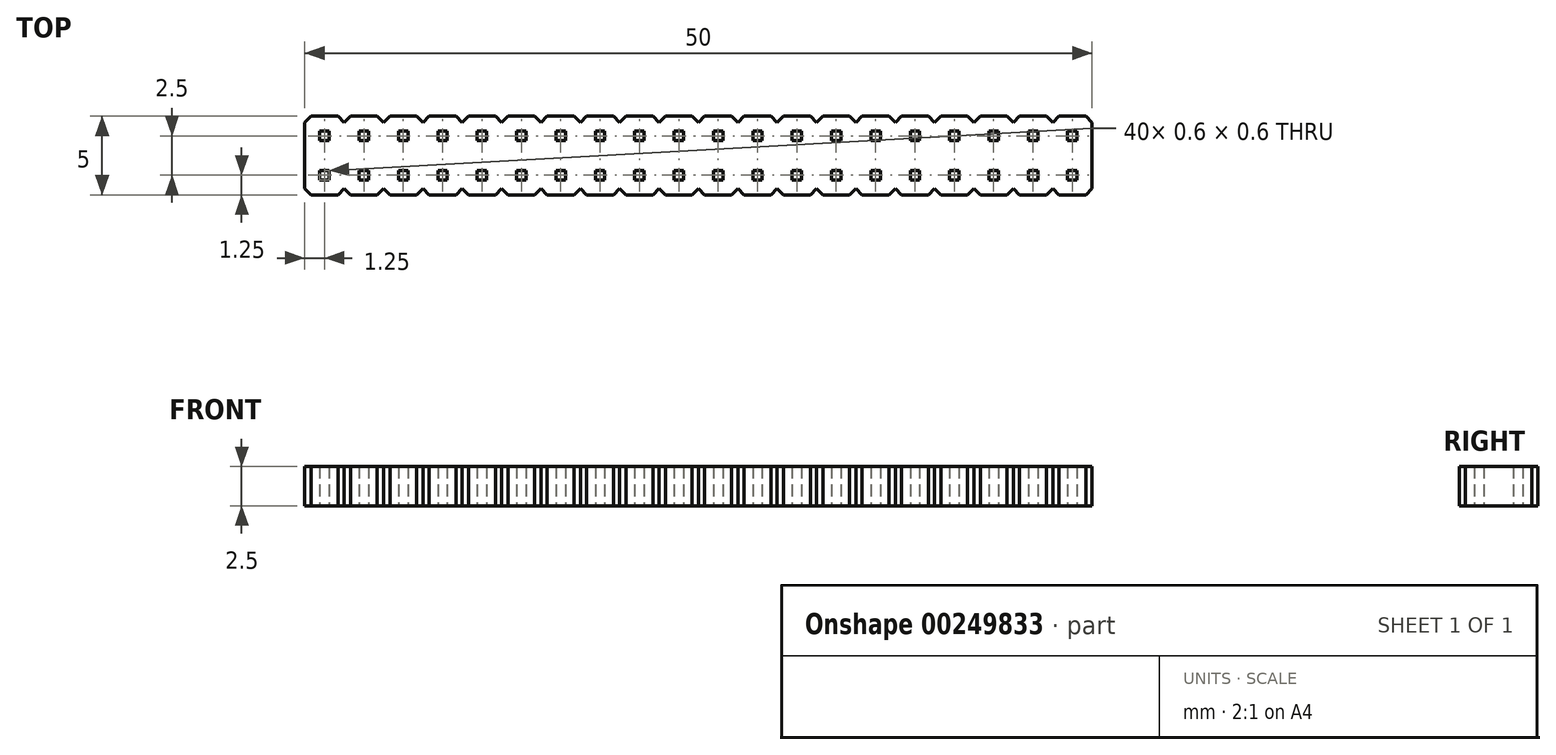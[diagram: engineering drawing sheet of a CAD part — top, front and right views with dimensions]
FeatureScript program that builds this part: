
annotation { "Feature Type Name" : "Feature", "Feature Type Description" : "" }
export const myFeature = defineFeature(function(context is Context, id is Id, definition is map)
    precondition{}
    {
        {
            var Q0;
            Q0=qCreatedBy(makeId("Top.planeOp"),FACE);
            var sketch = newSketch(context, id + "F0", { "sketchPlane" : qUnion([Q0])});
            skLineSegment(sketch, "E0.bottom", {"start": v(0.4, 0) * mm, "end": v(2.1, 0) * mm});
            skLineSegment(sketch, "E0.top", {"start": v(0.4, 5) * mm, "end": v(2.1, 5) * mm});
            skLineSegment(sketch, "E0.left", {"start": v(0, 0.4) * mm, "end": v(0, 4.6) * mm});
            skLineSegment(sketch, "E0.right", {"start": v(50, 0.4) * mm, "end": v(50, 4.6) * mm});
            skLineSegment(sketch, "E1", {"start": v(25, 5) * mm, "end": v(25, 0) * mm, "construction": true});
            skLineSegment(sketch, "E2", {"start": v(0, 2.5) * mm, "end": v(50, 2.5) * mm, "construction": true});
            skLineSegment(sketch, "E3.bottom", {"start": v(0.95, 4.05) * mm, "end": v(1.55, 4.05) * mm});
            skLineSegment(sketch, "E3.top", {"start": v(0.95, 3.45) * mm, "end": v(1.55, 3.45) * mm});
            skLineSegment(sketch, "E3.left", {"start": v(0.95, 4.05) * mm, "end": v(0.95, 3.45) * mm});
            skLineSegment(sketch, "E3.right", {"start": v(1.55, 4.05) * mm, "end": v(1.55, 3.45) * mm});
            skLineSegment(sketch, "E4", {"start": v(0, 4.6) * mm, "end": v(0.4, 5) * mm});
            skLineSegment(sketch, "E5", {"start": v(2.5, 5) * mm, "end": v(2.5, 2.5) * mm, "construction": true});
            skLineSegment(sketch, "E6", {"start": v(2.1, 5) * mm, "end": v(2.5, 4.6) * mm});
            skLineSegment(sketch, "E7.1.0.0", {"start": v(3.45, 3.45) * mm, "end": v(4.05, 3.45) * mm});
            skLineSegment(sketch, "E7.1.0.1", {"start": v(3.45, 4.05) * mm, "end": v(3.45, 3.45) * mm});
            skLineSegment(sketch, "E7.1.0.2", {"start": v(4.05, 4.05) * mm, "end": v(4.05, 3.45) * mm});
            skLineSegment(sketch, "E7.1.0.3", {"start": v(3.45, 4.05) * mm, "end": v(4.05, 4.05) * mm});
            skLineSegment(sketch, "E7.1.0.4", {"start": v(2.5, 4.6) * mm, "end": v(2.9, 5) * mm});
            skLineSegment(sketch, "E7.1.0.5", {"start": v(4.6, 5) * mm, "end": v(5, 4.6) * mm});
            skLineSegment(sketch, "E7.2.0.0", {"start": v(5.95, 3.45) * mm, "end": v(6.55, 3.45) * mm});
            skLineSegment(sketch, "E7.2.0.1", {"start": v(5.95, 4.05) * mm, "end": v(5.95, 3.45) * mm});
            skLineSegment(sketch, "E7.2.0.2", {"start": v(6.55, 4.05) * mm, "end": v(6.55, 3.45) * mm});
            skLineSegment(sketch, "E7.2.0.3", {"start": v(5.95, 4.05) * mm, "end": v(6.55, 4.05) * mm});
            skLineSegment(sketch, "E7.2.0.4", {"start": v(5, 4.6) * mm, "end": v(5.4, 5) * mm});
            skLineSegment(sketch, "E7.2.0.5", {"start": v(7.1, 5) * mm, "end": v(7.5, 4.6) * mm});
            skLineSegment(sketch, "E7.3.0.0", {"start": v(8.45, 3.45) * mm, "end": v(9.05, 3.45) * mm});
            skLineSegment(sketch, "E7.3.0.1", {"start": v(8.45, 4.05) * mm, "end": v(8.45, 3.45) * mm});
            skLineSegment(sketch, "E7.3.0.2", {"start": v(9.05, 4.05) * mm, "end": v(9.05, 3.45) * mm});
            skLineSegment(sketch, "E7.3.0.3", {"start": v(8.45, 4.05) * mm, "end": v(9.05, 4.05) * mm});
            skLineSegment(sketch, "E7.3.0.4", {"start": v(7.5, 4.6) * mm, "end": v(7.9, 5) * mm});
            skLineSegment(sketch, "E7.3.0.5", {"start": v(9.6, 5) * mm, "end": v(10, 4.6) * mm});
            skLineSegment(sketch, "E7.4.0.0", {"start": v(10.95, 3.45) * mm, "end": v(11.55, 3.45) * mm});
            skLineSegment(sketch, "E7.4.0.1", {"start": v(10.95, 4.05) * mm, "end": v(10.95, 3.45) * mm});
            skLineSegment(sketch, "E7.4.0.2", {"start": v(11.55, 4.05) * mm, "end": v(11.55, 3.45) * mm});
            skLineSegment(sketch, "E7.4.0.3", {"start": v(10.95, 4.05) * mm, "end": v(11.55, 4.05) * mm});
            skLineSegment(sketch, "E7.4.0.4", {"start": v(10, 4.6) * mm, "end": v(10.4, 5) * mm});
            skLineSegment(sketch, "E7.4.0.5", {"start": v(12.1, 5) * mm, "end": v(12.5, 4.6) * mm});
            skLineSegment(sketch, "E7.5.0.0", {"start": v(13.45, 3.45) * mm, "end": v(14.05, 3.45) * mm});
            skLineSegment(sketch, "E7.5.0.1", {"start": v(13.45, 4.05) * mm, "end": v(13.45, 3.45) * mm});
            skLineSegment(sketch, "E7.5.0.2", {"start": v(14.05, 4.05) * mm, "end": v(14.05, 3.45) * mm});
            skLineSegment(sketch, "E7.5.0.3", {"start": v(13.45, 4.05) * mm, "end": v(14.05, 4.05) * mm});
            skLineSegment(sketch, "E7.5.0.4", {"start": v(12.5, 4.6) * mm, "end": v(12.9, 5) * mm});
            skLineSegment(sketch, "E7.5.0.5", {"start": v(14.6, 5) * mm, "end": v(15, 4.6) * mm});
            skLineSegment(sketch, "E7.6.0.0", {"start": v(15.95, 3.45) * mm, "end": v(16.55, 3.45) * mm});
            skLineSegment(sketch, "E7.6.0.1", {"start": v(15.95, 4.05) * mm, "end": v(15.95, 3.45) * mm});
            skLineSegment(sketch, "E7.6.0.2", {"start": v(16.55, 4.05) * mm, "end": v(16.55, 3.45) * mm});
            skLineSegment(sketch, "E7.6.0.3", {"start": v(15.95, 4.05) * mm, "end": v(16.55, 4.05) * mm});
            skLineSegment(sketch, "E7.6.0.4", {"start": v(15, 4.6) * mm, "end": v(15.4, 5) * mm});
            skLineSegment(sketch, "E7.6.0.5", {"start": v(17.1, 5) * mm, "end": v(17.5, 4.6) * mm});
            skLineSegment(sketch, "E7.7.0.0", {"start": v(18.45, 3.45) * mm, "end": v(19.05, 3.45) * mm});
            skLineSegment(sketch, "E7.7.0.1", {"start": v(18.45, 4.05) * mm, "end": v(18.45, 3.45) * mm});
            skLineSegment(sketch, "E7.7.0.2", {"start": v(19.05, 4.05) * mm, "end": v(19.05, 3.45) * mm});
            skLineSegment(sketch, "E7.7.0.3", {"start": v(18.45, 4.05) * mm, "end": v(19.05, 4.05) * mm});
            skLineSegment(sketch, "E7.7.0.4", {"start": v(17.5, 4.6) * mm, "end": v(17.9, 5) * mm});
            skLineSegment(sketch, "E7.7.0.5", {"start": v(19.6, 5) * mm, "end": v(20, 4.6) * mm});
            skLineSegment(sketch, "E7.8.0.0", {"start": v(20.95, 3.45) * mm, "end": v(21.55, 3.45) * mm});
            skLineSegment(sketch, "E7.8.0.1", {"start": v(20.95, 4.05) * mm, "end": v(20.95, 3.45) * mm});
            skLineSegment(sketch, "E7.8.0.2", {"start": v(21.55, 4.05) * mm, "end": v(21.55, 3.45) * mm});
            skLineSegment(sketch, "E7.8.0.3", {"start": v(20.95, 4.05) * mm, "end": v(21.55, 4.05) * mm});
            skLineSegment(sketch, "E7.8.0.4", {"start": v(20, 4.6) * mm, "end": v(20.4, 5) * mm});
            skLineSegment(sketch, "E7.8.0.5", {"start": v(22.1, 5) * mm, "end": v(22.5, 4.6) * mm});
            skLineSegment(sketch, "E7.9.0.0", {"start": v(23.45, 3.45) * mm, "end": v(24.05, 3.45) * mm});
            skLineSegment(sketch, "E7.9.0.1", {"start": v(23.45, 4.05) * mm, "end": v(23.45, 3.45) * mm});
            skLineSegment(sketch, "E7.9.0.2", {"start": v(24.05, 4.05) * mm, "end": v(24.05, 3.45) * mm});
            skLineSegment(sketch, "E7.9.0.3", {"start": v(23.45, 4.05) * mm, "end": v(24.05, 4.05) * mm});
            skLineSegment(sketch, "E7.9.0.4", {"start": v(22.5, 4.6) * mm, "end": v(22.9, 5) * mm});
            skLineSegment(sketch, "E7.9.0.5", {"start": v(24.6, 5) * mm, "end": v(25, 4.6) * mm});
            skLineSegment(sketch, "E7.direction1", {"start": v(0.95, 3.45) * mm, "end": v(3.45, 3.45) * mm, "construction": true});
            skLineSegment(sketch, "E8.MirrorCS", {"start": v(23.45, 0.95) * mm, "end": v(24.05, 0.95) * mm});
            skLineSegment(sketch, "E9.MirrorCS", {"start": v(20.95, 1.55) * mm, "end": v(21.55, 1.55) * mm});
            skLineSegment(sketch, "E10.MirrorCS", {"start": v(23.45, 1.55) * mm, "end": v(24.05, 1.55) * mm});
            skLineSegment(sketch, "E11.MirrorCS", {"start": v(20.95, 0.95) * mm, "end": v(21.55, 0.95) * mm});
            skLineSegment(sketch, "E12.MirrorCS", {"start": v(0.95, 1.55) * mm, "end": v(1.55, 1.55) * mm});
            skLineSegment(sketch, "E13.MirrorCS", {"start": v(10.95, 0.95) * mm, "end": v(11.55, 0.95) * mm});
            skLineSegment(sketch, "E14.MirrorCS", {"start": v(18.45, 0.95) * mm, "end": v(18.45, 1.55) * mm});
            skLineSegment(sketch, "E15.MirrorCS", {"start": v(8.45, 1.55) * mm, "end": v(9.05, 1.55) * mm});
            skLineSegment(sketch, "E16.MirrorCS", {"start": v(21.55, 0.95) * mm, "end": v(21.55, 1.55) * mm});
            skLineSegment(sketch, "E17.MirrorCS", {"start": v(11.55, 0.95) * mm, "end": v(11.55, 1.55) * mm});
            skLineSegment(sketch, "E18.MirrorCS", {"start": v(18.45, 1.55) * mm, "end": v(19.05, 1.55) * mm});
            skLineSegment(sketch, "E19.MirrorCS", {"start": v(13.45, 0.95) * mm, "end": v(14.05, 0.95) * mm});
            skLineSegment(sketch, "E20.MirrorCS", {"start": v(20.95, 0.95) * mm, "end": v(20.95, 1.55) * mm});
            skLineSegment(sketch, "E21.MirrorCS", {"start": v(10.95, 0.95) * mm, "end": v(10.95, 1.55) * mm});
            skLineSegment(sketch, "E22.MirrorCS", {"start": v(3.45, 0.95) * mm, "end": v(4.05, 0.95) * mm});
            skLineSegment(sketch, "E23.MirrorCS", {"start": v(14.05, 0.95) * mm, "end": v(14.05, 1.55) * mm});
            skLineSegment(sketch, "E24.MirrorCS", {"start": v(1.55, 0.95) * mm, "end": v(1.55, 1.55) * mm});
            skLineSegment(sketch, "E25.MirrorCS", {"start": v(0.95, 0.95) * mm, "end": v(0.95, 1.55) * mm});
            skLineSegment(sketch, "E26.MirrorCS", {"start": v(0.95, 0.95) * mm, "end": v(1.55, 0.95) * mm});
            skLineSegment(sketch, "E27.MirrorCS", {"start": v(4.05, 0.95) * mm, "end": v(4.05, 1.55) * mm});
            skLineSegment(sketch, "E28.MirrorCS", {"start": v(3.45, 0.95) * mm, "end": v(3.45, 1.55) * mm});
            skLineSegment(sketch, "E29.MirrorCS", {"start": v(3.45, 1.55) * mm, "end": v(4.05, 1.55) * mm});
            skLineSegment(sketch, "E30.MirrorCS", {"start": v(13.45, 0.95) * mm, "end": v(13.45, 1.55) * mm});
            skLineSegment(sketch, "E31.MirrorCS", {"start": v(10.95, 1.55) * mm, "end": v(11.55, 1.55) * mm});
            skLineSegment(sketch, "E32.MirrorCS", {"start": v(24.05, 0.95) * mm, "end": v(24.05, 1.55) * mm});
            skLineSegment(sketch, "E33.MirrorCS", {"start": v(5.95, 0.95) * mm, "end": v(6.55, 0.95) * mm});
            skLineSegment(sketch, "E34.MirrorCS", {"start": v(13.45, 1.55) * mm, "end": v(14.05, 1.55) * mm});
            skLineSegment(sketch, "E35.MirrorCS", {"start": v(15.95, 0.95) * mm, "end": v(16.55, 0.95) * mm});
            skLineSegment(sketch, "E36.MirrorCS", {"start": v(23.45, 0.95) * mm, "end": v(23.45, 1.55) * mm});
            skLineSegment(sketch, "E37.MirrorCS", {"start": v(6.55, 0.95) * mm, "end": v(6.55, 1.55) * mm});
            skLineSegment(sketch, "E38.MirrorCS", {"start": v(8.45, 0.95) * mm, "end": v(9.05, 0.95) * mm});
            skLineSegment(sketch, "E39.MirrorCS", {"start": v(15.95, 0.95) * mm, "end": v(15.95, 1.55) * mm});
            skLineSegment(sketch, "E40.MirrorCS", {"start": v(18.45, 0.95) * mm, "end": v(19.05, 0.95) * mm});
            skLineSegment(sketch, "E41.MirrorCS", {"start": v(16.55, 0.95) * mm, "end": v(16.55, 1.55) * mm});
            skLineSegment(sketch, "E42.MirrorCS", {"start": v(15.95, 1.55) * mm, "end": v(16.55, 1.55) * mm});
            skLineSegment(sketch, "E43.MirrorCS", {"start": v(9.05, 0.95) * mm, "end": v(9.05, 1.55) * mm});
            skLineSegment(sketch, "E44.MirrorCS", {"start": v(5.95, 0.95) * mm, "end": v(5.95, 1.55) * mm});
            skLineSegment(sketch, "E45.MirrorCS", {"start": v(19.05, 0.95) * mm, "end": v(19.05, 1.55) * mm});
            skLineSegment(sketch, "E46.MirrorCS", {"start": v(8.45, 0.95) * mm, "end": v(8.45, 1.55) * mm});
            skLineSegment(sketch, "E47.MirrorCS", {"start": v(5.95, 1.55) * mm, "end": v(6.55, 1.55) * mm});
            skLineSegment(sketch, "E48.MirrorCS", {"start": v(0.95, 1.55) * mm, "end": v(3.45, 1.55) * mm, "construction": true});
            skLineSegment(sketch, "E49.MirrorCS", {"start": v(0, 0.4) * mm, "end": v(0.4, 0) * mm});
            skLineSegment(sketch, "E50.MirrorCS", {"start": v(2.1, 0) * mm, "end": v(2.5, 0.4) * mm});
            skLineSegment(sketch, "E51.MirrorCS", {"start": v(2.5, 0.4) * mm, "end": v(2.9, 0) * mm});
            skLineSegment(sketch, "E52.MirrorCS", {"start": v(4.6, 0) * mm, "end": v(5, 0.4) * mm});
            skLineSegment(sketch, "E53.MirrorCS", {"start": v(5, 0.4) * mm, "end": v(5.4, 0) * mm});
            skLineSegment(sketch, "E54.MirrorCS", {"start": v(7.1, 0) * mm, "end": v(7.5, 0.4) * mm});
            skLineSegment(sketch, "E55.MirrorCS", {"start": v(7.5, 0.4) * mm, "end": v(7.9, 0) * mm});
            skLineSegment(sketch, "E56.MirrorCS", {"start": v(9.6, 0) * mm, "end": v(10, 0.4) * mm});
            skLineSegment(sketch, "E57.MirrorCS", {"start": v(10, 0.4) * mm, "end": v(10.4, 0) * mm});
            skLineSegment(sketch, "E58.MirrorCS", {"start": v(12.1, 0) * mm, "end": v(12.5, 0.4) * mm});
            skLineSegment(sketch, "E59.MirrorCS", {"start": v(12.5, 0.4) * mm, "end": v(12.9, 0) * mm});
            skLineSegment(sketch, "E60.MirrorCS", {"start": v(14.6, 0) * mm, "end": v(15, 0.4) * mm});
            skLineSegment(sketch, "E61.MirrorCS", {"start": v(15, 0.4) * mm, "end": v(15.4, 0) * mm});
            skLineSegment(sketch, "E62.MirrorCS", {"start": v(17.1, 0) * mm, "end": v(17.5, 0.4) * mm});
            skLineSegment(sketch, "E63.MirrorCS", {"start": v(17.5, 0.4) * mm, "end": v(17.9, 0) * mm});
            skLineSegment(sketch, "E64.MirrorCS", {"start": v(19.6, 0) * mm, "end": v(20, 0.4) * mm});
            skLineSegment(sketch, "E65.MirrorCS", {"start": v(20, 0.4) * mm, "end": v(20.4, 0) * mm});
            skLineSegment(sketch, "E66.MirrorCS", {"start": v(22.1, 0) * mm, "end": v(22.5, 0.4) * mm});
            skLineSegment(sketch, "E67.MirrorCS", {"start": v(22.5, 0.4) * mm, "end": v(22.9, 0) * mm});
            skLineSegment(sketch, "E68.MirrorCS", {"start": v(24.6, 0) * mm, "end": v(25, 0.4) * mm});
            skLineSegment(sketch, "E69.MirrorCS", {"start": v(49.05, 1.55) * mm, "end": v(48.45, 1.55) * mm});
            skLineSegment(sketch, "E70.MirrorCS", {"start": v(49.05, 3.45) * mm, "end": v(48.45, 3.45) * mm});
            skLineSegment(sketch, "E71.MirrorCS", {"start": v(41.55, 0.95) * mm, "end": v(40.95, 0.95) * mm});
            skLineSegment(sketch, "E72.MirrorCS", {"start": v(39.05, 4.05) * mm, "end": v(38.45, 4.05) * mm});
            skLineSegment(sketch, "E73.MirrorCS", {"start": v(31.55, 4.05) * mm, "end": v(31.55, 3.45) * mm});
            skLineSegment(sketch, "E74.MirrorCS", {"start": v(46.55, 0.95) * mm, "end": v(45.95, 0.95) * mm});
            skLineSegment(sketch, "E75.MirrorCS", {"start": v(44.05, 3.45) * mm, "end": v(43.45, 3.45) * mm});
            skLineSegment(sketch, "E76.MirrorCS", {"start": v(35.95, 0.95) * mm, "end": v(35.95, 1.55) * mm});
            skLineSegment(sketch, "E77.MirrorCS", {"start": v(49.05, 3.45) * mm, "end": v(46.55, 3.45) * mm, "construction": true});
            skLineSegment(sketch, "E78.MirrorCS", {"start": v(30.95, 4.05) * mm, "end": v(30.95, 3.45) * mm});
            skLineSegment(sketch, "E79.MirrorCS", {"start": v(34.05, 0.95) * mm, "end": v(34.05, 1.55) * mm});
            skLineSegment(sketch, "E80.MirrorCS", {"start": v(49.05, 1.55) * mm, "end": v(46.55, 1.55) * mm, "construction": true});
            skLineSegment(sketch, "E81.MirrorCS", {"start": v(25.95, 0.95) * mm, "end": v(25.95, 1.55) * mm});
            skLineSegment(sketch, "E82.MirrorCS", {"start": v(28.45, 0.95) * mm, "end": v(28.45, 1.55) * mm});
            skLineSegment(sketch, "E83.MirrorCS", {"start": v(41.55, 4.05) * mm, "end": v(40.95, 4.05) * mm});
            skLineSegment(sketch, "E84.MirrorCS", {"start": v(43.45, 0.95) * mm, "end": v(43.45, 1.55) * mm});
            skLineSegment(sketch, "E85.MirrorCS", {"start": v(38.45, 4.05) * mm, "end": v(38.45, 3.45) * mm});
            skLineSegment(sketch, "E86.MirrorCS", {"start": v(31.55, 3.45) * mm, "end": v(30.95, 3.45) * mm});
            skLineSegment(sketch, "E87.MirrorCS", {"start": v(31.55, 1.55) * mm, "end": v(30.95, 1.55) * mm});
            skLineSegment(sketch, "E88.MirrorCS", {"start": v(34.05, 4.05) * mm, "end": v(33.45, 4.05) * mm});
            skLineSegment(sketch, "E89.MirrorCS", {"start": v(39.05, 0.95) * mm, "end": v(39.05, 1.55) * mm});
            skLineSegment(sketch, "E90.MirrorCS", {"start": v(34.05, 4.05) * mm, "end": v(34.05, 3.45) * mm});
            skLineSegment(sketch, "E91.MirrorCS", {"start": v(39.05, 4.05) * mm, "end": v(39.05, 3.45) * mm});
            skLineSegment(sketch, "E92.MirrorCS", {"start": v(44.05, 0.95) * mm, "end": v(43.45, 0.95) * mm});
            skLineSegment(sketch, "E93.MirrorCS", {"start": v(26.55, 4.05) * mm, "end": v(25.95, 4.05) * mm});
            skLineSegment(sketch, "E94.MirrorCS", {"start": v(29.05, 0.95) * mm, "end": v(29.05, 1.55) * mm});
            skLineSegment(sketch, "E95.MirrorCS", {"start": v(46.55, 4.05) * mm, "end": v(45.95, 4.05) * mm});
            skLineSegment(sketch, "E96.MirrorCS", {"start": v(33.45, 4.05) * mm, "end": v(33.45, 3.45) * mm});
            skLineSegment(sketch, "E97.MirrorCS", {"start": v(26.55, 3.45) * mm, "end": v(25.95, 3.45) * mm});
            skLineSegment(sketch, "E98.MirrorCS", {"start": v(38.45, 0.95) * mm, "end": v(38.45, 1.55) * mm});
            skLineSegment(sketch, "E99.MirrorCS", {"start": v(41.55, 1.55) * mm, "end": v(40.95, 1.55) * mm});
            skLineSegment(sketch, "E100.MirrorCS", {"start": v(39.05, 1.55) * mm, "end": v(38.45, 1.55) * mm});
            skLineSegment(sketch, "E101.MirrorCS", {"start": v(44.05, 1.55) * mm, "end": v(43.45, 1.55) * mm});
            skLineSegment(sketch, "E102.MirrorCS", {"start": v(40.95, 4.05) * mm, "end": v(40.95, 3.45) * mm});
            skLineSegment(sketch, "E103.MirrorCS", {"start": v(34.05, 3.45) * mm, "end": v(33.45, 3.45) * mm});
            skLineSegment(sketch, "E104.MirrorCS", {"start": v(26.55, 0.95) * mm, "end": v(26.55, 1.55) * mm});
            skLineSegment(sketch, "E105.MirrorCS", {"start": v(26.55, 4.05) * mm, "end": v(26.55, 3.45) * mm});
            skLineSegment(sketch, "E106.MirrorCS", {"start": v(44.05, 4.05) * mm, "end": v(44.05, 3.45) * mm});
            skLineSegment(sketch, "E107.MirrorCS", {"start": v(48.45, 0.95) * mm, "end": v(48.45, 1.55) * mm});
            skLineSegment(sketch, "E108.MirrorCS", {"start": v(26.55, 0.95) * mm, "end": v(25.95, 0.95) * mm});
            skLineSegment(sketch, "E109.MirrorCS", {"start": v(31.55, 4.05) * mm, "end": v(30.95, 4.05) * mm});
            skLineSegment(sketch, "E110.MirrorCS", {"start": v(36.55, 1.55) * mm, "end": v(35.95, 1.55) * mm});
            skLineSegment(sketch, "E111.MirrorCS", {"start": v(31.55, 0.95) * mm, "end": v(30.95, 0.95) * mm});
            skLineSegment(sketch, "E112.MirrorCS", {"start": v(36.55, 0.95) * mm, "end": v(36.55, 1.55) * mm});
            skLineSegment(sketch, "E113.MirrorCS", {"start": v(43.45, 4.05) * mm, "end": v(43.45, 3.45) * mm});
            skLineSegment(sketch, "E114.MirrorCS", {"start": v(49.05, 0.95) * mm, "end": v(49.05, 1.55) * mm});
            skLineSegment(sketch, "E115.MirrorCS", {"start": v(29.05, 1.55) * mm, "end": v(28.45, 1.55) * mm});
            skLineSegment(sketch, "E116.MirrorCS", {"start": v(36.55, 0.95) * mm, "end": v(35.95, 0.95) * mm});
            skLineSegment(sketch, "E117.MirrorCS", {"start": v(25.95, 4.05) * mm, "end": v(25.95, 3.45) * mm});
            skLineSegment(sketch, "E118.MirrorCS", {"start": v(36.55, 3.45) * mm, "end": v(35.95, 3.45) * mm});
            skLineSegment(sketch, "E119.MirrorCS", {"start": v(39.05, 3.45) * mm, "end": v(38.45, 3.45) * mm});
            skLineSegment(sketch, "E120.MirrorCS", {"start": v(33.45, 0.95) * mm, "end": v(33.45, 1.55) * mm});
            skLineSegment(sketch, "E121.MirrorCS", {"start": v(34.05, 0.95) * mm, "end": v(33.45, 0.95) * mm});
            skLineSegment(sketch, "E122.MirrorCS", {"start": v(46.55, 3.45) * mm, "end": v(45.95, 3.45) * mm});
            skLineSegment(sketch, "E123.MirrorCS", {"start": v(46.55, 4.05) * mm, "end": v(46.55, 3.45) * mm});
            skLineSegment(sketch, "E124.MirrorCS", {"start": v(45.95, 4.05) * mm, "end": v(45.95, 3.45) * mm});
            skLineSegment(sketch, "E125.MirrorCS", {"start": v(49.05, 0.95) * mm, "end": v(48.45, 0.95) * mm});
            skLineSegment(sketch, "E126.MirrorCS", {"start": v(44.05, 4.05) * mm, "end": v(43.45, 4.05) * mm});
            skLineSegment(sketch, "E127.MirrorCS", {"start": v(26.55, 1.55) * mm, "end": v(25.95, 1.55) * mm});
            skLineSegment(sketch, "E128.MirrorCS", {"start": v(36.55, 4.05) * mm, "end": v(36.55, 3.45) * mm});
            skLineSegment(sketch, "E129.MirrorCS", {"start": v(34.05, 1.55) * mm, "end": v(33.45, 1.55) * mm});
            skLineSegment(sketch, "E130.MirrorCS", {"start": v(35.95, 4.05) * mm, "end": v(35.95, 3.45) * mm});
            skLineSegment(sketch, "E131.MirrorCS", {"start": v(29.05, 3.45) * mm, "end": v(28.45, 3.45) * mm});
            skLineSegment(sketch, "E132.MirrorCS", {"start": v(45.95, 0.95) * mm, "end": v(45.95, 1.55) * mm});
            skLineSegment(sketch, "E133.MirrorCS", {"start": v(29.05, 0.95) * mm, "end": v(28.45, 0.95) * mm});
            skLineSegment(sketch, "E134.MirrorCS", {"start": v(40.95, 0.95) * mm, "end": v(40.95, 1.55) * mm});
            skLineSegment(sketch, "E135.MirrorCS", {"start": v(36.55, 4.05) * mm, "end": v(35.95, 4.05) * mm});
            skLineSegment(sketch, "E136.MirrorCS", {"start": v(29.05, 4.05) * mm, "end": v(29.05, 3.45) * mm});
            skLineSegment(sketch, "E137.MirrorCS", {"start": v(44.05, 0.95) * mm, "end": v(44.05, 1.55) * mm});
            skLineSegment(sketch, "E138.MirrorCS", {"start": v(46.55, 0.95) * mm, "end": v(46.55, 1.55) * mm});
            skLineSegment(sketch, "E139.MirrorCS", {"start": v(28.45, 4.05) * mm, "end": v(28.45, 3.45) * mm});
            skLineSegment(sketch, "E140.MirrorCS", {"start": v(46.55, 1.55) * mm, "end": v(45.95, 1.55) * mm});
            skLineSegment(sketch, "E141.MirrorCS", {"start": v(31.55, 0.95) * mm, "end": v(31.55, 1.55) * mm});
            skLineSegment(sketch, "E142.MirrorCS", {"start": v(41.55, 3.45) * mm, "end": v(40.95, 3.45) * mm});
            skLineSegment(sketch, "E143.MirrorCS", {"start": v(30.95, 0.95) * mm, "end": v(30.95, 1.55) * mm});
            skLineSegment(sketch, "E144.MirrorCS", {"start": v(49.05, 4.05) * mm, "end": v(49.05, 3.45) * mm});
            skLineSegment(sketch, "E145.MirrorCS", {"start": v(48.45, 4.05) * mm, "end": v(48.45, 3.45) * mm});
            skLineSegment(sketch, "E146.MirrorCS", {"start": v(39.05, 0.95) * mm, "end": v(38.45, 0.95) * mm});
            skLineSegment(sketch, "E147.MirrorCS", {"start": v(41.55, 0.95) * mm, "end": v(41.55, 1.55) * mm});
            skLineSegment(sketch, "E148.MirrorCS", {"start": v(49.05, 4.05) * mm, "end": v(48.45, 4.05) * mm});
            skLineSegment(sketch, "E149.MirrorCS", {"start": v(41.55, 4.05) * mm, "end": v(41.55, 3.45) * mm});
            skLineSegment(sketch, "E150.MirrorCS", {"start": v(29.05, 4.05) * mm, "end": v(28.45, 4.05) * mm});
            skLineSegment(sketch, "E151.MirrorCS", {"start": v(50, 4.6) * mm, "end": v(49.6, 5) * mm});
            skLineSegment(sketch, "E152.MirrorCS", {"start": v(50, 0.4) * mm, "end": v(49.6, 0) * mm});
            skLineSegment(sketch, "E153.MirrorCS", {"start": v(47.9, 5) * mm, "end": v(47.5, 4.6) * mm});
            skLineSegment(sketch, "E154.MirrorCS", {"start": v(47.9, 0) * mm, "end": v(47.5, 0.4) * mm});
            skLineSegment(sketch, "E155.MirrorCS", {"start": v(47.5, 4.6) * mm, "end": v(47.1, 5) * mm});
            skLineSegment(sketch, "E156.MirrorCS", {"start": v(47.5, 0.4) * mm, "end": v(47.1, 0) * mm});
            skLineSegment(sketch, "E157.MirrorCS", {"start": v(45.4, 0) * mm, "end": v(45, 0.4) * mm});
            skLineSegment(sketch, "E158.MirrorCS", {"start": v(45.4, 5) * mm, "end": v(45, 4.6) * mm});
            skLineSegment(sketch, "E159.MirrorCS", {"start": v(45, 4.6) * mm, "end": v(44.6, 5) * mm});
            skLineSegment(sketch, "E160.MirrorCS", {"start": v(45, 0.4) * mm, "end": v(44.6, 0) * mm});
            skLineSegment(sketch, "E161.MirrorCS", {"start": v(42.9, 5) * mm, "end": v(42.5, 4.6) * mm});
            skLineSegment(sketch, "E162.MirrorCS", {"start": v(42.9, 0) * mm, "end": v(42.5, 0.4) * mm});
            skLineSegment(sketch, "E163.MirrorCS", {"start": v(42.5, 4.6) * mm, "end": v(42.1, 5) * mm});
            skLineSegment(sketch, "E164.MirrorCS", {"start": v(42.5, 0.4) * mm, "end": v(42.1, 0) * mm});
            skLineSegment(sketch, "E165.MirrorCS", {"start": v(40.4, 5) * mm, "end": v(40, 4.6) * mm});
            skLineSegment(sketch, "E166.MirrorCS", {"start": v(40.4, 0) * mm, "end": v(40, 0.4) * mm});
            skLineSegment(sketch, "E167.MirrorCS", {"start": v(40, 4.6) * mm, "end": v(39.6, 5) * mm});
            skLineSegment(sketch, "E168.MirrorCS", {"start": v(40, 0.4) * mm, "end": v(39.6, 0) * mm});
            skLineSegment(sketch, "E169.MirrorCS", {"start": v(37.9, 5) * mm, "end": v(37.5, 4.6) * mm});
            skLineSegment(sketch, "E170.MirrorCS", {"start": v(37.9, 0) * mm, "end": v(37.5, 0.4) * mm});
            skLineSegment(sketch, "E171.MirrorCS", {"start": v(37.5, 4.6) * mm, "end": v(37.1, 5) * mm});
            skLineSegment(sketch, "E172.MirrorCS", {"start": v(37.5, 0.4) * mm, "end": v(37.1, 0) * mm});
            skLineSegment(sketch, "E173.MirrorCS", {"start": v(25.4, 5) * mm, "end": v(25, 4.6) * mm});
            skLineSegment(sketch, "E174.MirrorCS", {"start": v(25.4, 0) * mm, "end": v(25, 0.4) * mm});
            skLineSegment(sketch, "E175.MirrorCS", {"start": v(27.5, 0.4) * mm, "end": v(27.1, 0) * mm});
            skLineSegment(sketch, "E176.MirrorCS", {"start": v(27.5, 4.6) * mm, "end": v(27.1, 5) * mm});
            skLineSegment(sketch, "E177.MirrorCS", {"start": v(27.9, 5) * mm, "end": v(27.5, 4.6) * mm});
            skLineSegment(sketch, "E178.MirrorCS", {"start": v(27.9, 0) * mm, "end": v(27.5, 0.4) * mm});
            skLineSegment(sketch, "E179.MirrorCS", {"start": v(30, 0.4) * mm, "end": v(29.6, 0) * mm});
            skLineSegment(sketch, "E180.MirrorCS", {"start": v(30, 4.6) * mm, "end": v(29.6, 5) * mm});
            skLineSegment(sketch, "E181.MirrorCS", {"start": v(30.4, 5) * mm, "end": v(30, 4.6) * mm});
            skLineSegment(sketch, "E182.MirrorCS", {"start": v(30.4, 0) * mm, "end": v(30, 0.4) * mm});
            skLineSegment(sketch, "E183.MirrorCS", {"start": v(32.5, 4.6) * mm, "end": v(32.1, 5) * mm});
            skLineSegment(sketch, "E184.MirrorCS", {"start": v(32.5, 0.4) * mm, "end": v(32.1, 0) * mm});
            skLineSegment(sketch, "E185.MirrorCS", {"start": v(32.9, 0) * mm, "end": v(32.5, 0.4) * mm});
            skLineSegment(sketch, "E186.MirrorCS", {"start": v(32.9, 5) * mm, "end": v(32.5, 4.6) * mm});
            skLineSegment(sketch, "E187.MirrorCS", {"start": v(35, 4.6) * mm, "end": v(34.6, 5) * mm});
            skLineSegment(sketch, "E188.MirrorCS", {"start": v(35, 0.4) * mm, "end": v(34.6, 0) * mm});
            skLineSegment(sketch, "E189.MirrorCS", {"start": v(35.4, 5) * mm, "end": v(35, 4.6) * mm});
            skLineSegment(sketch, "E190.MirrorCS", {"start": v(35.4, 0) * mm, "end": v(35, 0.4) * mm});
            skPoint(sketch, "E191.orphan", {"position": v(0, 5) * mm});
            skLineSegment(sketch, "E192.trimOffspring", {"start": v(2.9, 5) * mm, "end": v(4.6, 5) * mm});
            skLineSegment(sketch, "E193.trimOffspring", {"start": v(5.4, 5) * mm, "end": v(7.1, 5) * mm});
            skLineSegment(sketch, "E194.trimOffspring", {"start": v(7.9, 5) * mm, "end": v(9.6, 5) * mm});
            skLineSegment(sketch, "E195.trimOffspring", {"start": v(10.4, 5) * mm, "end": v(12.1, 5) * mm});
            skLineSegment(sketch, "E196.trimOffspring", {"start": v(12.9, 5) * mm, "end": v(14.6, 5) * mm});
            skLineSegment(sketch, "E197.trimOffspring", {"start": v(15.4, 5) * mm, "end": v(17.1, 5) * mm});
            skLineSegment(sketch, "E198.trimOffspring", {"start": v(17.9, 5) * mm, "end": v(19.6, 5) * mm});
            skLineSegment(sketch, "E199.trimOffspring", {"start": v(20.4, 5) * mm, "end": v(22.1, 5) * mm});
            skLineSegment(sketch, "E200.trimOffspring", {"start": v(22.9, 5) * mm, "end": v(24.6, 5) * mm});
            skLineSegment(sketch, "E201.trimOffspring", {"start": v(25.4, 5) * mm, "end": v(27.1, 5) * mm});
            skLineSegment(sketch, "E202.trimOffspring", {"start": v(27.9, 5) * mm, "end": v(29.6, 5) * mm});
            skLineSegment(sketch, "E203.trimOffspring", {"start": v(30.4, 5) * mm, "end": v(32.1, 5) * mm});
            skLineSegment(sketch, "E204.trimOffspring", {"start": v(32.9, 5) * mm, "end": v(34.6, 5) * mm});
            skLineSegment(sketch, "E205.trimOffspring", {"start": v(35.4, 5) * mm, "end": v(37.1, 5) * mm});
            skLineSegment(sketch, "E206.trimOffspring", {"start": v(37.9, 5) * mm, "end": v(39.6, 5) * mm});
            skLineSegment(sketch, "E207.trimOffspring", {"start": v(40.4, 5) * mm, "end": v(42.1, 5) * mm});
            skLineSegment(sketch, "E208.trimOffspring", {"start": v(42.9, 5) * mm, "end": v(44.6, 5) * mm});
            skLineSegment(sketch, "E209.trimOffspring", {"start": v(45.4, 5) * mm, "end": v(47.1, 5) * mm});
            skLineSegment(sketch, "E210.trimOffspring", {"start": v(47.9, 5) * mm, "end": v(49.6, 5) * mm});
            skPoint(sketch, "E211.orphan", {"position": v(50, 5) * mm});
            skPoint(sketch, "E212.orphan", {"position": v(50, 0) * mm});
            skLineSegment(sketch, "E213.trimOffspring", {"start": v(47.9, 0) * mm, "end": v(49.6, 0) * mm});
            skLineSegment(sketch, "E214.trimOffspring", {"start": v(45.4, 0) * mm, "end": v(47.1, 0) * mm});
            skLineSegment(sketch, "E215.trimOffspring", {"start": v(42.9, 0) * mm, "end": v(44.6, 0) * mm});
            skLineSegment(sketch, "E216.trimOffspring", {"start": v(40.4, 0) * mm, "end": v(42.1, 0) * mm});
            skLineSegment(sketch, "E217.trimOffspring", {"start": v(37.9, 0) * mm, "end": v(39.6, 0) * mm});
            skLineSegment(sketch, "E218.trimOffspring", {"start": v(35.4, 0) * mm, "end": v(37.1, 0) * mm});
            skLineSegment(sketch, "E219.trimOffspring", {"start": v(32.9, 0) * mm, "end": v(34.6, 0) * mm});
            skLineSegment(sketch, "E220.trimOffspring", {"start": v(30.4, 0) * mm, "end": v(32.1, 0) * mm});
            skLineSegment(sketch, "E221.trimOffspring", {"start": v(27.9, 0) * mm, "end": v(29.6, 0) * mm});
            skLineSegment(sketch, "E222.trimOffspring", {"start": v(25.4, 0) * mm, "end": v(27.1, 0) * mm});
            skLineSegment(sketch, "E223.trimOffspring", {"start": v(22.9, 0) * mm, "end": v(24.6, 0) * mm});
            skLineSegment(sketch, "E224.trimOffspring", {"start": v(20.4, 0) * mm, "end": v(22.1, 0) * mm});
            skLineSegment(sketch, "E225.trimOffspring", {"start": v(17.9, 0) * mm, "end": v(19.6, 0) * mm});
            skLineSegment(sketch, "E226.trimOffspring", {"start": v(15.4, 0) * mm, "end": v(17.1, 0) * mm});
            skPoint(sketch, "E227.orphan", {"position": v(0, 0) * mm});
            skLineSegment(sketch, "E228.trimOffspring", {"start": v(2.9, 0) * mm, "end": v(4.6, 0) * mm});
            skLineSegment(sketch, "E229.trimOffspring", {"start": v(5.4, 0) * mm, "end": v(7.1, 0) * mm});
            skLineSegment(sketch, "E230.trimOffspring", {"start": v(7.9, 0) * mm, "end": v(9.6, 0) * mm});
            skLineSegment(sketch, "E231.trimOffspring", {"start": v(10.4, 0) * mm, "end": v(12.1, 0) * mm});
            skLineSegment(sketch, "E232.trimOffspring", {"start": v(12.9, 0) * mm, "end": v(14.6, 0) * mm});
            skSolve(sketch);
        }
        {
            var Q0;
            Q0 = qSketchRegion(id + "F0", true);
            extrude(context, id + "F1", {"entities" : qUnion([Q0]), "depth" : 2.5 * mm});
        }
    });
